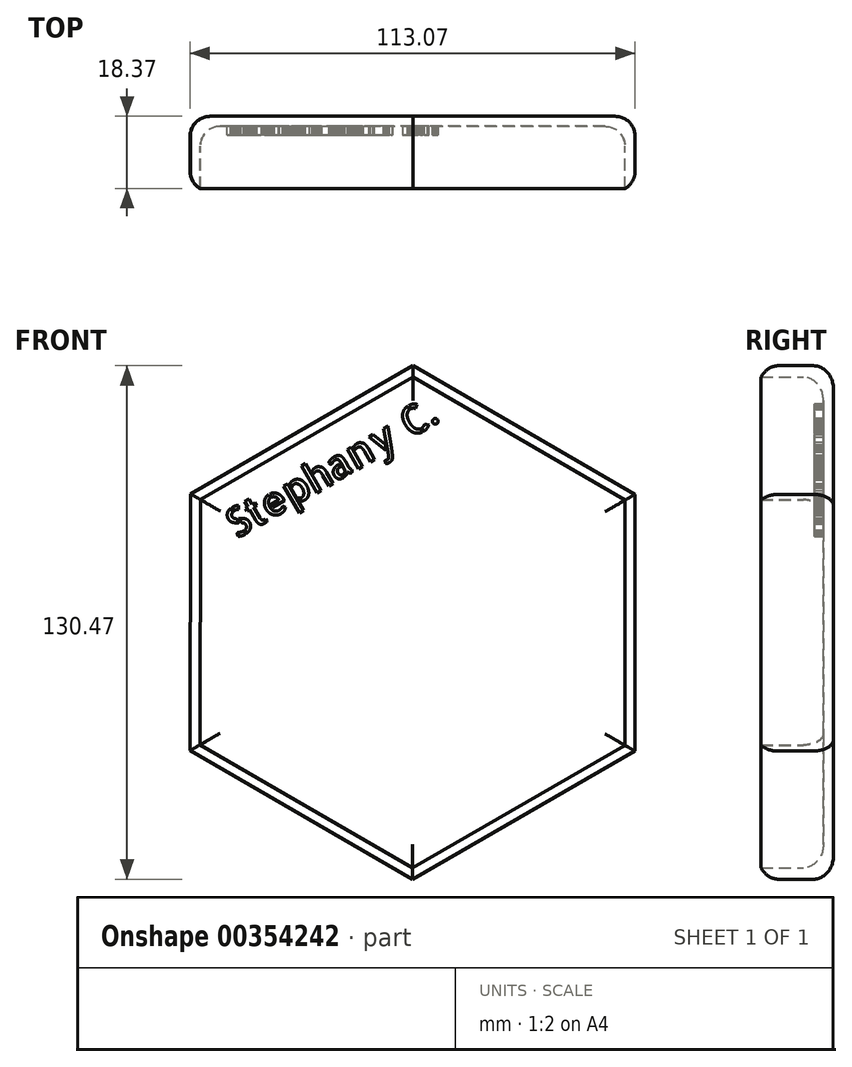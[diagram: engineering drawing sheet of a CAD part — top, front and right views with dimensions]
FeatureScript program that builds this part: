
annotation { "Feature Type Name" : "Feature", "Feature Type Description" : "" }
export const myFeature = defineFeature(function(context is Context, id is Id, definition is map)
    precondition{}
    {
        {
            var Q0;
            Q0=qCreatedBy(makeId("Front.planeOp"),FACE);
            var sketch = newSketch(context, id + "F0", { "sketchPlane" : qUnion([Q0])});
            skCircle(sketch, "E0.cCircle", {"center": v(-4.67, 7.85) * mm, "radius": 56.5 * mm, "construction": true});
            skLineSegment(sketch, "E0.0", {"start": v(51.78, -24.84) * mm, "end": v(-4.75, -57.39) * mm});
            skLineSegment(sketch, "E0.1", {"start": v(-4.75, -57.39) * mm, "end": v(-61.2, -24.7) * mm});
            skLineSegment(sketch, "E0.2", {"start": v(-61.2, -24.7) * mm, "end": v(-61.13, 40.53) * mm});
            skLineSegment(sketch, "E0.3", {"start": v(-61.13, 40.53) * mm, "end": v(-4.6, 73.08) * mm});
            skLineSegment(sketch, "E0.4", {"start": v(-4.6, 73.08) * mm, "end": v(51.86, 40.4) * mm});
            skLineSegment(sketch, "E0.5", {"start": v(51.86, 40.4) * mm, "end": v(51.78, -24.84) * mm});
            skPoint(sketch, "E0.0.midPoint", {"position": v(23.51, -41.11) * mm});
            skSolve(sketch);
        }
        {
            var Q0;
            Q0=makeQuery(id+"F0.imprint","IMPRINT",FACE,{"disambiguationData":[TD([[makeQuery(id+"F0.imprint","IMPRINT",EDGE,{"derivedFrom":sQuery(id+"F0.wireOp",EDGE,"E0.0")}),-1.0]])]});
            extrude(context, id + "F1", {"entities" : qUnion([Q0]), "depth" : 19.05 * mm});
        }
        {
            var Q0;
            Q0=makeQuery(id+"F1.opExtrude","CAP_FACE",FACE,{"disambiguationData":[OSD([sQuery(id+"F0.wireOp",EDGE,"E0.0"),sQuery(id+"F0.wireOp",EDGE,"E0.1"),sQuery(id+"F0.wireOp",EDGE,"E0.2"),sQuery(id+"F0.wireOp",EDGE,"E0.3"),sQuery(id+"F0.wireOp",EDGE,"E0.4"),sQuery(id+"F0.wireOp",EDGE,"E0.5")])],"isStart":false});
            shell(context, id + "F2", {"entities" : qUnion([Q0]), "thickness" : 2.54 * mm});
        }
        {
            var Q0;
            Q0=makeQuery(id+"F1.opExtrude","CAP_EDGE",EDGE,{"disambiguationData":[OSD([sQuery(id+"F0.wireOp",EDGE,"E0.2")])],"isStart":false});
            var Q1;
            Q1=makeQuery(id+"F1.opExtrude","CAP_EDGE",EDGE,{"disambiguationData":[OSD([sQuery(id+"F0.wireOp",EDGE,"E0.3")])],"isStart":false});
            var Q2;
            Q2=makeQuery(id+"F1.opExtrude","CAP_EDGE",EDGE,{"disambiguationData":[OSD([sQuery(id+"F0.wireOp",EDGE,"E0.4")])],"isStart":false});
            var Q3;
            Q3=makeQuery(id+"F1.opExtrude","CAP_EDGE",EDGE,{"disambiguationData":[OSD([sQuery(id+"F0.wireOp",EDGE,"E0.5")])],"isStart":false});
            var Q4;
            Q4=makeQuery(id+"F1.opExtrude","CAP_EDGE",EDGE,{"disambiguationData":[OSD([sQuery(id+"F0.wireOp",EDGE,"E0.0")])],"isStart":false});
            var Q5;
            Q5=makeQuery(id+"F1.opExtrude","CAP_EDGE",EDGE,{"disambiguationData":[OSD([sQuery(id+"F0.wireOp",EDGE,"E0.1")])],"isStart":false});
            var Q6;
            Q6=makeQuery(id+"F2.opShell","OFFSET_FACE",FACE,{"disambiguationData":[OSD([sQuery(id+"F0.wireOp",EDGE,"E0.0"),sQuery(id+"F0.wireOp",EDGE,"E0.1"),sQuery(id+"F0.wireOp",EDGE,"E0.2"),sQuery(id+"F0.wireOp",EDGE,"E0.3"),sQuery(id+"F0.wireOp",EDGE,"E0.4"),sQuery(id+"F0.wireOp",EDGE,"E0.5")])]});
            var Q7;
            Q7=makeQuery(id+"F1.opExtrude","CAP_EDGE",EDGE,{"disambiguationData":[OSD([sQuery(id+"F0.wireOp",EDGE,"E0.0")])],"isStart":true});
            var Q8;
            Q8=makeQuery(id+"F1.opExtrude","CAP_EDGE",EDGE,{"disambiguationData":[OSD([sQuery(id+"F0.wireOp",EDGE,"E0.5")])],"isStart":true});
            var Q9;
            Q9=makeQuery(id+"F1.opExtrude","CAP_EDGE",EDGE,{"disambiguationData":[OSD([sQuery(id+"F0.wireOp",EDGE,"E0.4")])],"isStart":true});
            var Q10;
            Q10=makeQuery(id+"F1.opExtrude","CAP_EDGE",EDGE,{"disambiguationData":[OSD([sQuery(id+"F0.wireOp",EDGE,"E0.3")])],"isStart":true});
            var Q11;
            Q11=makeQuery(id+"F1.opExtrude","CAP_EDGE",EDGE,{"disambiguationData":[OSD([sQuery(id+"F0.wireOp",EDGE,"E0.2")])],"isStart":true});
            var Q12;
            Q12=makeQuery(id+"F1.opExtrude","CAP_EDGE",EDGE,{"disambiguationData":[OSD([sQuery(id+"F0.wireOp",EDGE,"E0.1")])],"isStart":true});
            fillet(context, id + "F3", {"entities" : qUnion([Q0, Q1, Q2, Q3, Q4, Q5, Q6, Q7, Q8, Q9, Q10, Q11, Q12]), "radius" : 5.08 * mm, "tangentPropagation" : true, "allowEdgeOverflow" : false});
        }
        {
            var Q0;
            Q0=qCreatedBy(makeId("Front.planeOp"),FACE);
            var sketch = newSketch(context, id + "F4", { "sketchPlane" : qUnion([Q0])});
            skText(sketch, "E1", { "text": "Stephany C.", "fontName": "AllertaStencil-Regular.ttf"});
            const initialGuessF4  = {"E1": [-0.0495, 0.02894, 0.86603, 0.5, 0.00744]};
            skSetInitialGuess(sketch, initialGuessF4);
            skSolve(sketch);
        }
        {
            var Q0;
            Q0 = qSketchRegion(id + "F4", true);
            extrude(context, id + "F5", {"entities" : qUnion([Q0]), "operationType" : NewBodyOperationType.ADD, "depth" : 4.83 * mm});
        }
    });
